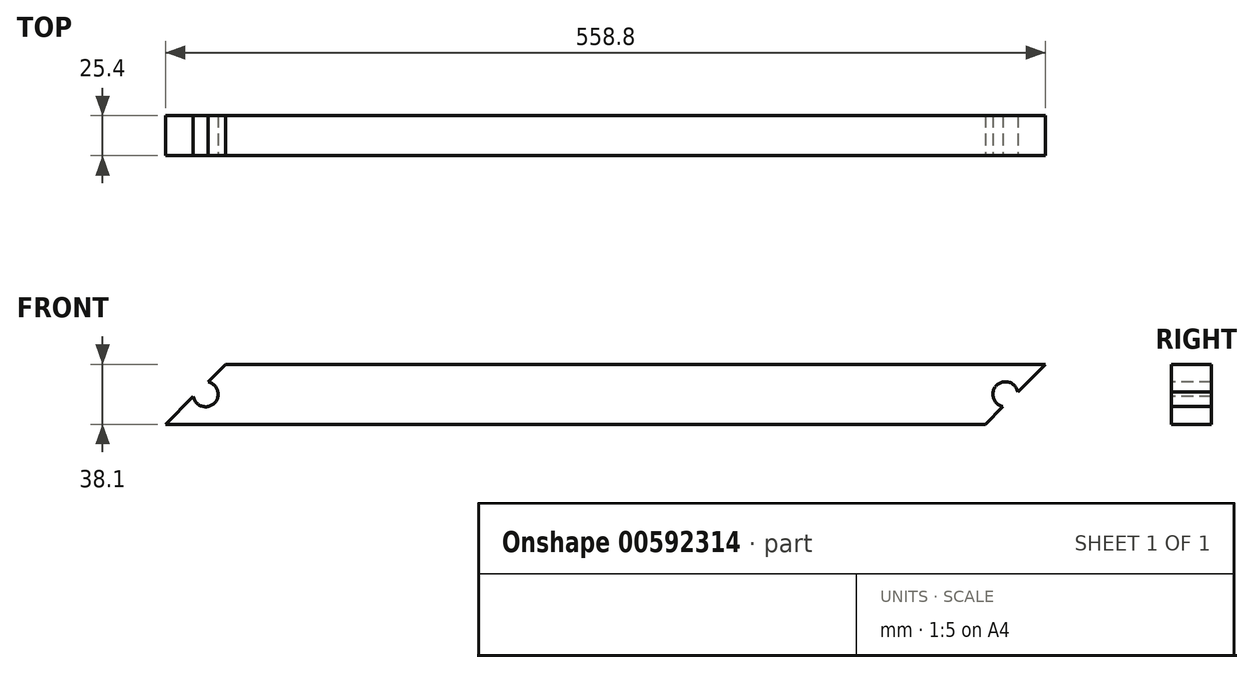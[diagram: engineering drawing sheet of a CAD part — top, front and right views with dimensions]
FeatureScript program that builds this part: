
annotation { "Feature Type Name" : "Feature", "Feature Type Description" : "" }
export const myFeature = defineFeature(function(context is Context, id is Id, definition is map)
    precondition{}
    {
        {
            var Q0;
            Q0=qCreatedBy(makeId("Front.planeOp"),FACE);
            var sketch = newSketch(context, id + "F0", { "sketchPlane" : qUnion([Q0])});
            skLineSegment(sketch, "E0.bottom", {"start": v(0, 0) * mm, "end": v(558.8, 0) * mm});
            skLineSegment(sketch, "E0.top", {"start": v(0, 38.1) * mm, "end": v(558.8, 38.1) * mm});
            skLineSegment(sketch, "E0.left", {"start": v(0, 0) * mm, "end": v(0, 38.1) * mm});
            skLineSegment(sketch, "E0.right", {"start": v(558.8, 0) * mm, "end": v(558.8, 38.1) * mm});
            skSolve(sketch);
        }
        {
            var Q0;
            Q0=makeQuery(id+"F0.imprint","IMPRINT",FACE,{"disambiguationData":[TD([[makeQuery(id+"F0.imprint","IMPRINT",EDGE,{"derivedFrom":sQuery(id+"F0.wireOp",EDGE,"E0.bottom")}),1.0]])]});
            extrude(context, id + "F1", {"entities" : qUnion([Q0]), "depth" : 25.4 * mm, "offsetDistance" : 25.4 * mm});
        }
        {
            var Q0;
            Q0=makeQuery(id+"F1.opExtrude","CAP_FACE",FACE,{"disambiguationData":[OSD([sQuery(id+"F0.wireOp",EDGE,"E0.bottom"),sQuery(id+"F0.wireOp",EDGE,"E0.top"),sQuery(id+"F0.wireOp",EDGE,"E0.left"),sQuery(id+"F0.wireOp",EDGE,"E0.right")])],"isStart":false});
            var sketch = newSketch(context, id + "F2", { "sketchPlane" : qUnion([Q0])});
            skCircle(sketch, "E1", {"center": v(25.4, 19.05) * mm, "radius": 6.35 * mm});
            skCircle(sketch, "E2", {"center": v(533.4, 19.05) * mm, "radius": 6.35 * mm});
            skSolve(sketch);
        }
        {
            var Q0;
            Q0=sQuery(id+"F2.wireOp",VERTEX,"E1.center");
            var Q1;
            Q1=sQuery(id+"F2.wireOp",VERTEX,"1KIZwOIM-GRpi-KB8x-ajEx-Oq6Q15zxiPFI.center");
            var Q2;
            Q2=sQuery(id+"F2.wireOp",VERTEX,"Mo5Y4d3M-FWyN-rOX8-mSTb-Zg6RNz9Z2ruR.center");
            var Q3;
            Q3=sQuery(id+"F2.wireOp",VERTEX,"E2.center");
            var Q4;
            Q4=makeQuery(id+"F1.opExtrude","SWEPT_BODY",BODY,{"disambiguationData":[OSD([sQuery(id+"F0.wireOp",EDGE,"E0.bottom"),sQuery(id+"F0.wireOp",EDGE,"E0.top"),sQuery(id+"F0.wireOp",EDGE,"E0.left"),sQuery(id+"F0.wireOp",EDGE,"E0.right")])]});
            hole(context, id + "F3", {"style" : HoleStyle.SIMPLE, "endStyle" : HoleEndStyle.THROUGH, "holeDiameter" : 15.88 * mm, "majorDiameter" : 6.35 * mm, "isTappedThrough" : true, "tappedDepth" : 12.7 * mm, "tapClearance" : 3, "locations" : qUnion([Q0, Q1, Q2, Q3]), "scope" : qUnion([Q4])});
        }
        {
            var Q0;
            Q0=makeQuery(id+"F1.opExtrude","CAP_FACE",FACE,{"disambiguationData":[OSD([sQuery(id+"F0.wireOp",EDGE,"E0.bottom"),sQuery(id+"F0.wireOp",EDGE,"E0.top"),sQuery(id+"F0.wireOp",EDGE,"E0.left"),sQuery(id+"F0.wireOp",EDGE,"E0.right")])],"isStart":false});
            var sketch = newSketch(context, id + "F4", { "sketchPlane" : qUnion([Q0])});
            skLineSegment(sketch, "E3", {"start": v(0, 0) * mm, "end": v(38.1, 38.1) * mm});
            skLineSegment(sketch, "E4", {"start": v(38.1, 38.1) * mm, "end": v(0, 38.1) * mm});
            skLineSegment(sketch, "E5", {"start": v(0, 38.1) * mm, "end": v(0, 0) * mm});
            skSolve(sketch);
        }
        {
            var Q0;
            Q0=makeQuery(id+"F4.imprint","IMPRINT",FACE,{"disambiguationData":[TD([[makeQuery(id+"F4.imprint","IMPRINT",EDGE,{"derivedFrom":sQuery(id+"F4.wireOp",EDGE,"E3")}),1.0]])]});
            extrude(context, id + "F5", {"entities" : qUnion([Q0]), "operationType" : NewBodyOperationType.REMOVE, "oppositeDirection" : true, "depth" : 50.8 * mm, "offsetDistance" : 25.4 * mm});
        }
        {
            var Q0;
            Q0=makeQuery(id+"F1.opExtrude","CAP_FACE",FACE,{"disambiguationData":[OSD([sQuery(id+"F0.wireOp",EDGE,"E0.bottom"),sQuery(id+"F0.wireOp",EDGE,"E0.top"),sQuery(id+"F0.wireOp",EDGE,"E0.left"),sQuery(id+"F0.wireOp",EDGE,"E0.right")])],"isStart":false});
            var sketch = newSketch(context, id + "F6", { "sketchPlane" : qUnion([Q0])});
            skLineSegment(sketch, "E6", {"start": v(558.8, 38.1) * mm, "end": v(520.7, 0) * mm});
            skLineSegment(sketch, "E7", {"start": v(520.7, 0) * mm, "end": v(558.8, 0) * mm});
            skLineSegment(sketch, "E8", {"start": v(558.8, 0) * mm, "end": v(558.8, 38.1) * mm});
            skSolve(sketch);
        }
        {
            var Q0;
            {var subQ1=sQuery(id+"F6.wireOp",EDGE,"E7");Q0=makeQuery(id+"F6.imprint","IMPRINT",FACE,{"disambiguationData":[TD([[makeQuery(id+"F6.imprint","IMPRINT",EDGE,{"derivedFrom":subQ1}),1.0]])]});}
            extrude(context, id + "F7", {"entities" : qUnion([Q0]), "operationType" : NewBodyOperationType.REMOVE, "oppositeDirection" : true, "depth" : 50.8 * mm, "offsetDistance" : 25.4 * mm});
        }
    });
